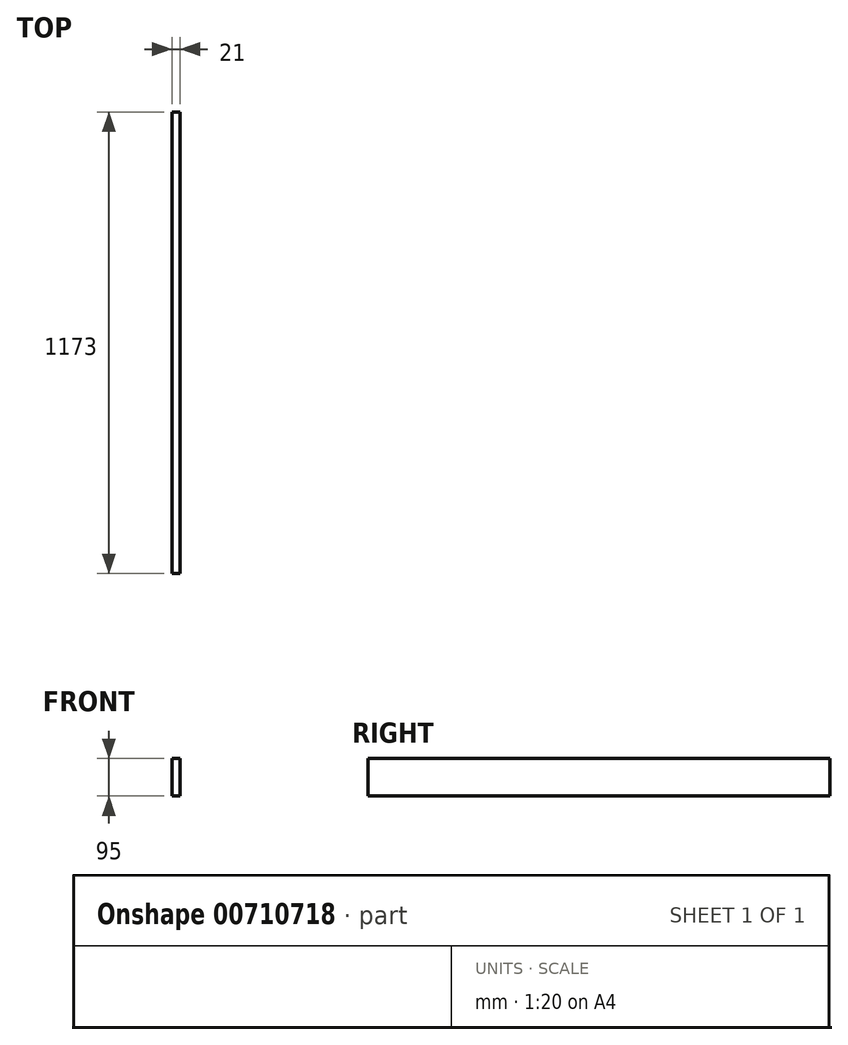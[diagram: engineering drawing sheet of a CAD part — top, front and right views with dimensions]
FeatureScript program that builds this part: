
annotation { "Feature Type Name" : "Feature", "Feature Type Description" : "" }
export const myFeature = defineFeature(function(context is Context, id is Id, definition is map)
    precondition{}
    {
        {
            assignVariable(context, id + "F0", {"name" : "l", "anyValue" : 1215 - 42});
        }
        {
            var Q0;
            Q0=qCreatedBy(makeId("Front.planeOp"),FACE);
            var sketch = newSketch(context, id + "F1", { "sketchPlane" : qUnion([Q0])});
            skLineSegment(sketch, "E0.bottom", {"start": v(0, 0) * mm, "end": v(21, 0) * mm});
            skLineSegment(sketch, "E0.top", {"start": v(0, 95) * mm, "end": v(21, 95) * mm});
            skLineSegment(sketch, "E0.left", {"start": v(0, 0) * mm, "end": v(0, 95) * mm});
            skLineSegment(sketch, "E0.right", {"start": v(21, 0) * mm, "end": v(21, 95) * mm});
            skSolve(sketch);
        }
        {
            var Q0;
            Q0 = qSketchRegion(id + "F1", true);
            extrude(context, id + "F2", {"entities" : qUnion([Q0]), "depth" : (getVariable(context, 'l')) * mm, "offsetDistance" : 25 * mm});
        }
    });
